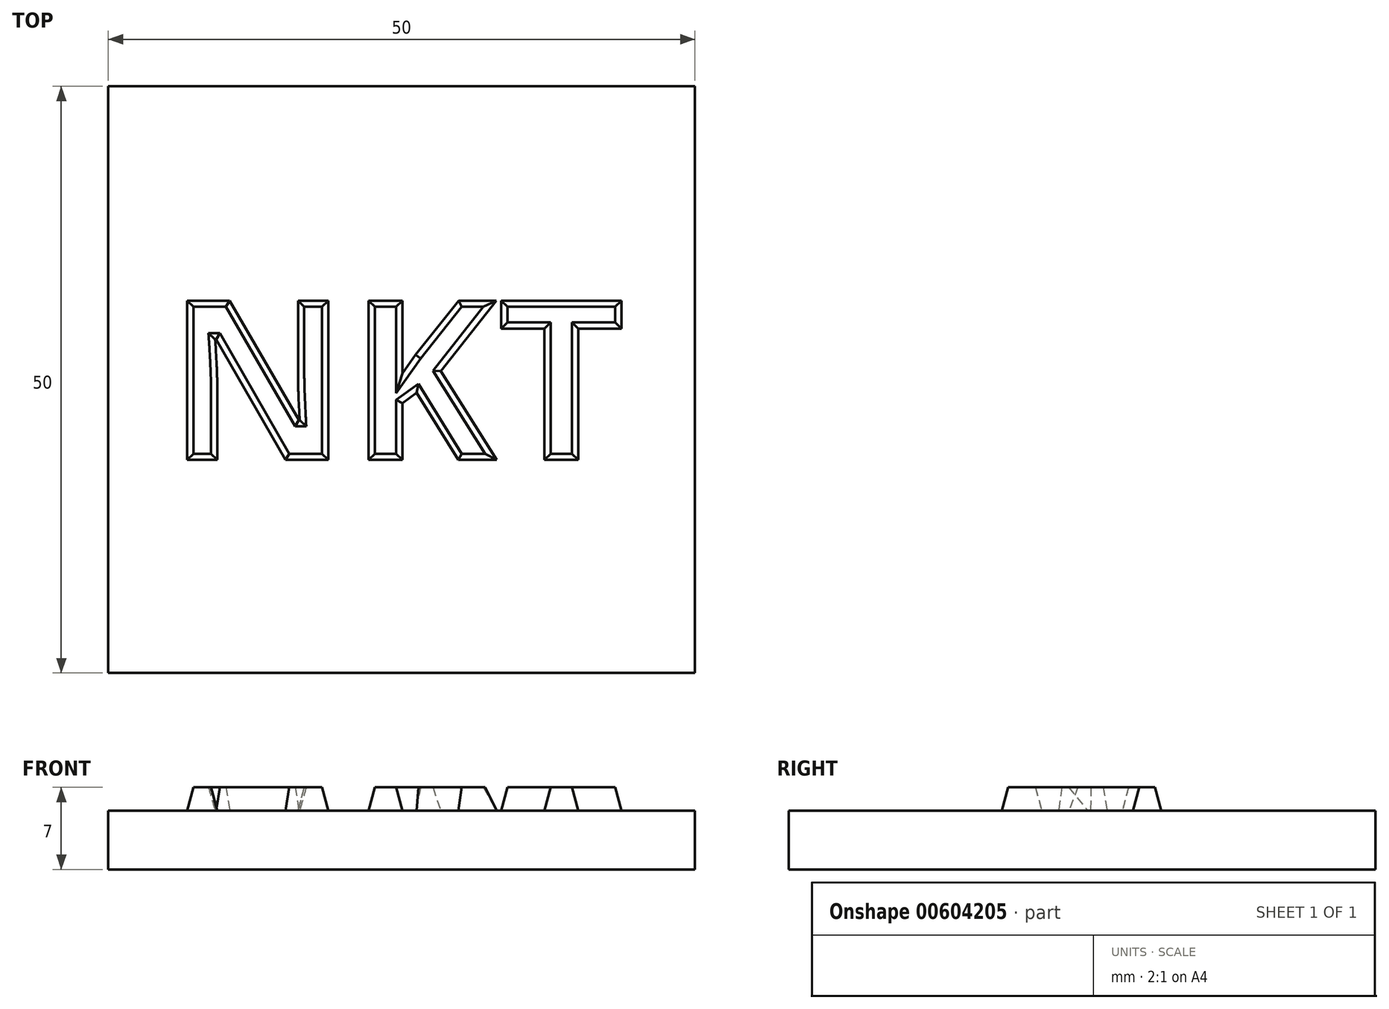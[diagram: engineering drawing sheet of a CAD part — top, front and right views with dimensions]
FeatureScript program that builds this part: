
annotation { "Feature Type Name" : "Feature", "Feature Type Description" : "" }
export const myFeature = defineFeature(function(context is Context, id is Id, definition is map)
    precondition{}
    {
        {
            var Q0;
            Q0=qCreatedBy(makeId("Top.planeOp"),FACE);
            var sketch = newSketch(context, id + "F0", { "sketchPlane" : qUnion([Q0])});
            skLineSegment(sketch, "E0.bottom", {"start": v(-25, 25) * mm, "end": v(25, 25) * mm});
            skLineSegment(sketch, "E0.top", {"start": v(-25, -25) * mm, "end": v(25, -25) * mm});
            skLineSegment(sketch, "E0.left", {"start": v(-25, 25) * mm, "end": v(-25, -25) * mm});
            skLineSegment(sketch, "E0.right", {"start": v(25, 25) * mm, "end": v(25, -25) * mm});
            skSolve(sketch);
        }
        {
            var Q0;
            Q0 = qSketchRegion(id + "F0", true);
            extrude(context, id + "F1", {"entities" : qUnion([Q0]), "depth" : 5 * mm, "offsetDistance" : 25 * mm});
        }
        {
            var Q0;
            Q0=makeQuery(id+"F1.opExtrude","CAP_FACE",FACE,{"disambiguationData":[OSD([sQuery(id+"F0.wireOp",EDGE,"E0.bottom"),sQuery(id+"F0.wireOp",EDGE,"E0.top"),sQuery(id+"F0.wireOp",EDGE,"E0.left"),sQuery(id+"F0.wireOp",EDGE,"E0.right")])],"isStart":false});
            var sketch = newSketch(context, id + "F2", { "sketchPlane" : qUnion([Q0])});
            skText(sketch, "E1", { "text": "NKT", "fontName": "NotoSans-Bold.ttf"});
            const initialGuessF2  = {"E1": [-0.02, -0.00685, 1, 0, 0.0137]};
            skSetInitialGuess(sketch, initialGuessF2);
            skSolve(sketch);
        }
        {
            var Q0;
            Q0 = qSketchRegion(id + "F2", true);
            extrude(context, id + "F3", {"entities" : qUnion([Q0]), "operationType" : NewBodyOperationType.ADD, "depth" : 2 * mm, "offsetDistance" : 25 * mm, "hasDraft" : true, "draftAngle" : 15 * degree, "draftPullDirection" : true});
        }
    });
